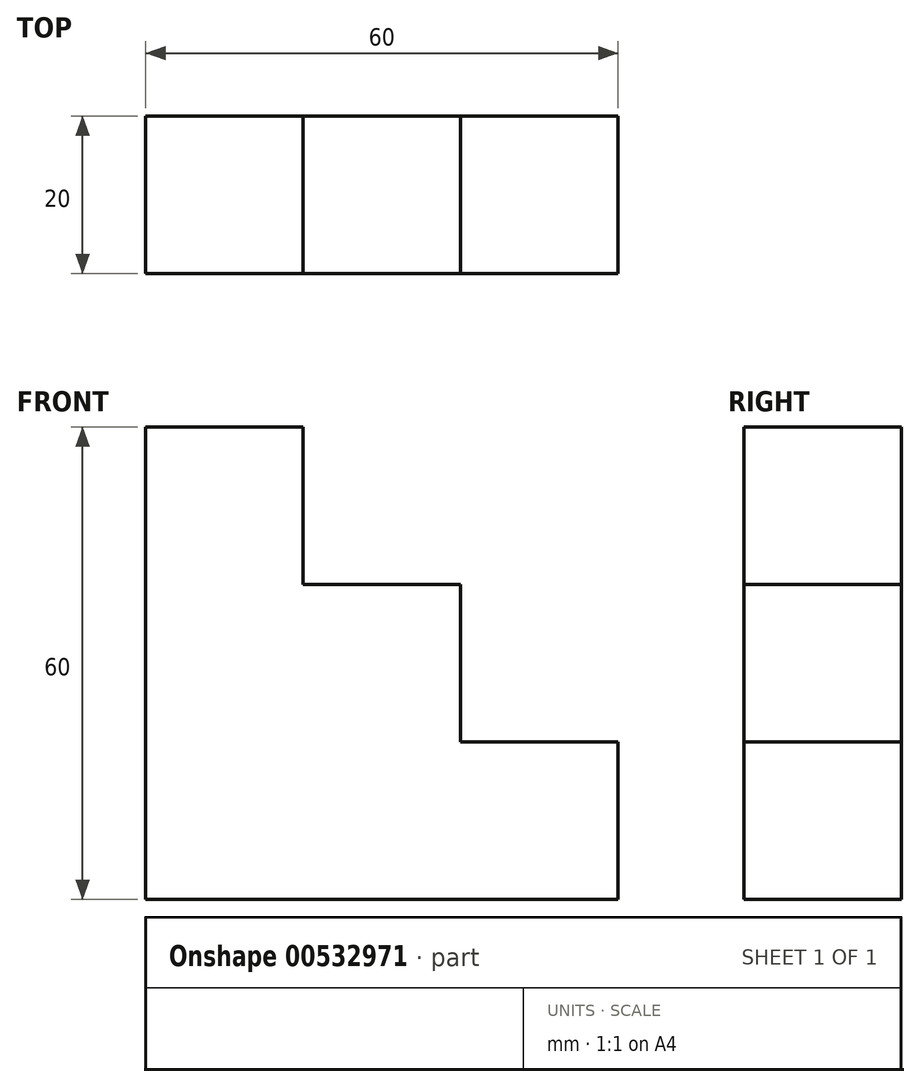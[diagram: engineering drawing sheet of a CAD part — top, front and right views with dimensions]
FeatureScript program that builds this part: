
annotation { "Feature Type Name" : "Feature", "Feature Type Description" : "" }
export const myFeature = defineFeature(function(context is Context, id is Id, definition is map)
    precondition{}
    {
        {
            var Q0;
            Q0=qCreatedBy(makeId("Front.planeOp"),FACE);
            var sketch = newSketch(context, id + "F0", { "sketchPlane" : qUnion([Q0])});
            skLineSegment(sketch, "E0", {"start": v(-31.6, 20) * mm, "end": v(-31.6, -40) * mm});
            skLineSegment(sketch, "E1", {"start": v(-31.6, -40) * mm, "end": v(28.4, -40) * mm});
            skLineSegment(sketch, "E2", {"start": v(28.4, -40) * mm, "end": v(28.4, -20) * mm});
            skLineSegment(sketch, "E3", {"start": v(28.4, -20) * mm, "end": v(8.4, -20) * mm});
            skLineSegment(sketch, "E4", {"start": v(8.4, -20) * mm, "end": v(8.4, 0) * mm});
            skLineSegment(sketch, "E5", {"start": v(8.4, 0) * mm, "end": v(-11.6, 0) * mm});
            skLineSegment(sketch, "E6", {"start": v(-11.6, 0) * mm, "end": v(-11.6, 20) * mm});
            skLineSegment(sketch, "E7", {"start": v(-11.6, 20) * mm, "end": v(-31.6, 20) * mm});
            skSolve(sketch);
        }
        {
            var Q0;
            Q0 = qSketchRegion(id + "F0", true);
            extrude(context, id + "F1", {"entities" : qUnion([Q0]), "depth" : 20 * mm, "offsetDistance" : 25 * mm});
        }
    });
